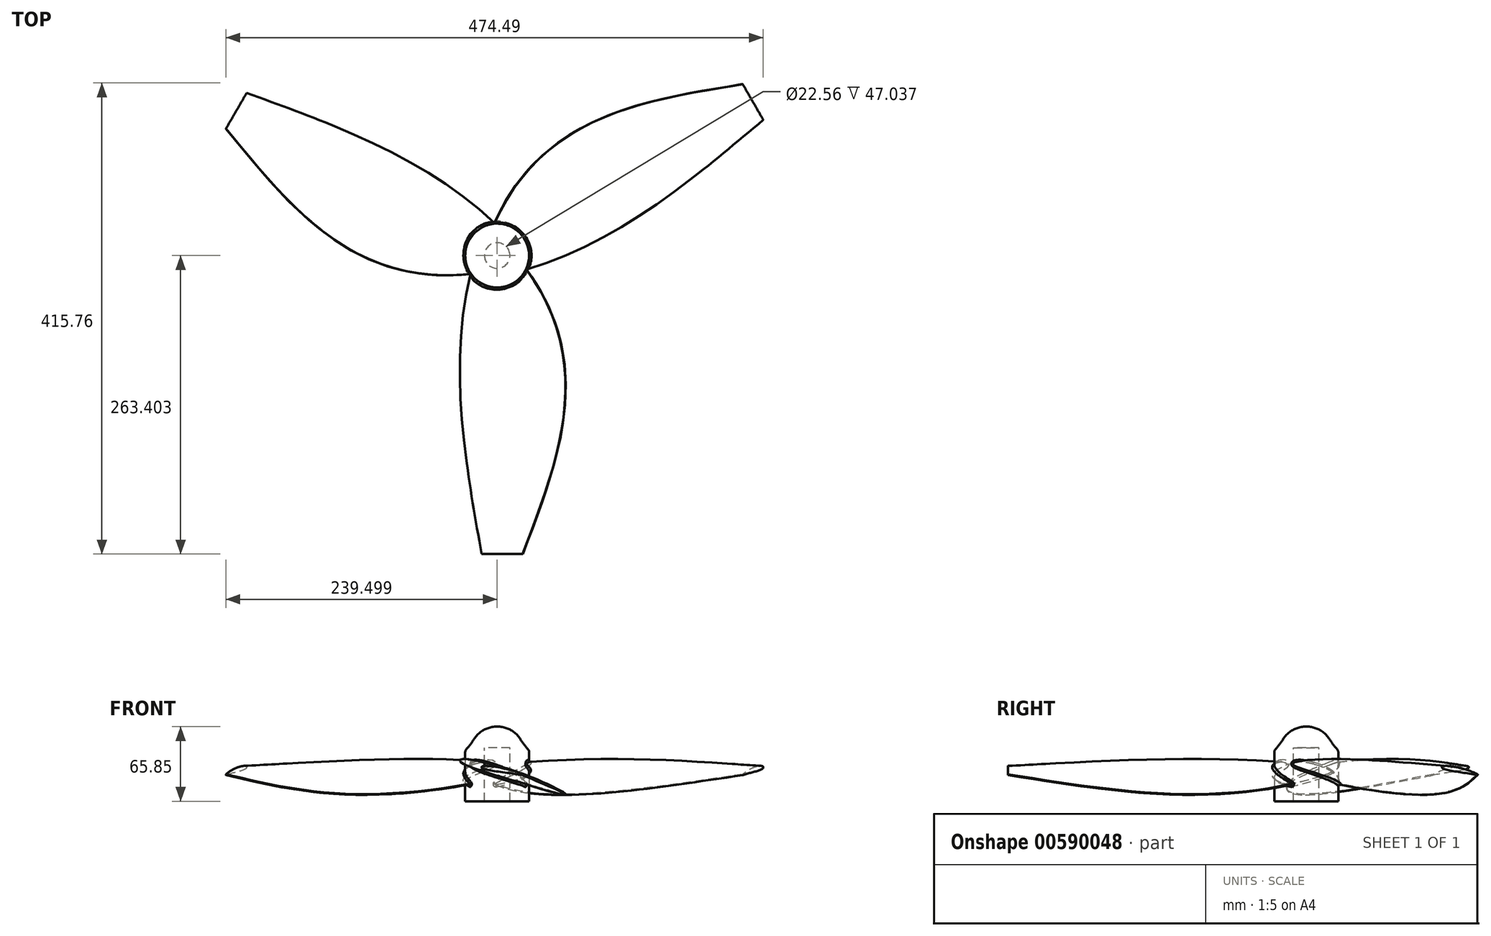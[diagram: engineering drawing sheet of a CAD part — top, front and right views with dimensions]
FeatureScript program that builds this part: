
annotation { "Feature Type Name" : "Feature", "Feature Type Description" : "" }
export const myFeature = defineFeature(function(context is Context, id is Id, definition is map)
    precondition{}
    {
        {
            var Q0;
            Q0=qCreatedBy(makeId("Front.planeOp"),FACE);
            var sketch = newSketch(context, id + "F0", { "sketchPlane" : qUnion([Q0])});
            skLineSegment(sketch, "E0", {"start": v(-25.68, 10.16) * mm, "end": v(0, 0) * mm, "construction": true});
            skLineSegment(sketch, "E1", {"start": v(0, 0) * mm, "end": v(25.68, -10.16) * mm, "construction": true});
            skLineSegment(sketch, "E2", {"start": v(25.68, -10.16) * mm, "end": v(51.36, -20.31) * mm, "construction": true});
            skLineSegment(sketch, "E3", {"start": v(51.36, -20.31) * mm, "end": v(77.03, -30.47) * mm, "construction": true});
            skLineSegment(sketch, "E4", {"start": v(0, 0) * mm, "end": v(3.73, 9.44) * mm, "construction": true});
            skLineSegment(sketch, "E5", {"start": v(-25.68, 10.16) * mm, "end": v(-23.81, 14.88) * mm, "construction": true});
            skFitSpline(sketch, "E6", {"points": [v(-25.68, 10.16) * mm, v(3.73, 9.44) * mm, v(77.03, -30.47) * mm], "startDerivative": vector(15.03, 38) * mm, "endDerivative": vector(104.92, -93.69) * mm});
            skPoint(sketch, "E7", {"position": v(1.87, 4.72) * mm});
            skLineSegment(sketch, "E8", {"start": v(-23.81, 14.88) * mm, "end": v(1.87, 4.72) * mm, "construction": true});
            skLineSegment(sketch, "E9", {"start": v(0, 0) * mm, "end": v(-1.87, -4.72) * mm, "construction": true});
            skLineSegment(sketch, "E10", {"start": v(-25.68, 10.16) * mm, "end": v(-27.54, 5.44) * mm, "construction": true});
            skFitSpline(sketch, "E11", {"points": [v(-25.68, 10.16) * mm, v(-1.87, -4.72) * mm, v(77.03, -30.47) * mm], "startDerivative": vector(-15.23, -38.5) * mm, "endDerivative": vector(121.84, -48.19) * mm});
            skLineSegment(sketch, "E12", {"start": v(51.36, -20.31) * mm, "end": v(55.09, -10.87) * mm, "construction": true});
            skSolve(sketch);
        }
        {
            var Q0;
            Q0=qCreatedBy(makeId("Front.planeOp"),FACE);
            cPlane(context, id + "F1", {"entities" : qUnion([Q0]), "cplaneType" : CPlaneType.OFFSET, "offset" : 50.8 * mm, "width" : 150 * mm, "height" : 150 * mm});
        }
        {
            var Q0;
            Q0=qCreatedBy(id+"F1.planeOp",FACE);
            var sketch = newSketch(context, id + "F2", { "sketchPlane" : qUnion([Q0])});
            skLineSegment(sketch, "E13", {"start": v(-38.33, 14.06) * mm, "end": v(0, 0) * mm, "construction": true});
            skLineSegment(sketch, "E14", {"start": v(0, 0) * mm, "end": v(38.33, -14.06) * mm, "construction": true});
            skLineSegment(sketch, "E15", {"start": v(38.33, -14.06) * mm, "end": v(76.67, -28.12) * mm, "construction": true});
            skLineSegment(sketch, "E16", {"start": v(76.67, -28.12) * mm, "end": v(115, -42.17) * mm, "construction": true});
            skLineSegment(sketch, "E17", {"start": v(0, 0) * mm, "end": v(4.06, 11.06) * mm, "construction": true});
            skLineSegment(sketch, "E18", {"start": v(-38.33, 14.06) * mm, "end": v(-36.3, 19.59) * mm, "construction": true});
            skFitSpline(sketch, "E19", {"points": [v(-38.33, 14.06) * mm, v(4.06, 11.06) * mm, v(115, -42.17) * mm], "startDerivative": vector(16.44, 44.82) * mm, "endDerivative": vector(163.27, -119.63) * mm});
            skPoint(sketch, "E20", {"position": v(2.03, 5.53) * mm});
            skLineSegment(sketch, "E21", {"start": v(-36.3, 19.59) * mm, "end": v(2.03, 5.53) * mm, "construction": true});
            skLineSegment(sketch, "E22", {"start": v(0, 0) * mm, "end": v(-2.03, -5.53) * mm, "construction": true});
            skLineSegment(sketch, "E23", {"start": v(-38.33, 14.06) * mm, "end": v(-40.36, 8.53) * mm, "construction": true});
            skFitSpline(sketch, "E24", {"points": [v(-38.33, 14.06) * mm, v(-2.03, -5.53) * mm, v(115, -42.17) * mm], "startDerivative": vector(-16.57, -45.19) * mm, "endDerivative": vector(181.7, -66.64) * mm});
            skLineSegment(sketch, "E25", {"start": v(76.67, -28.12) * mm, "end": v(80.72, -17.06) * mm, "construction": true});
            skSolve(sketch);
        }
        {
            var Q0;
            Q0=qCreatedBy(makeId("Front.planeOp"),FACE);
            cPlane(context, id + "F3", {"entities" : qUnion([Q0]), "cplaneType" : CPlaneType.OFFSET, "offset" : 711.2 * mm, "width" : 150 * mm, "height" : 150 * mm});
        }
        {
            var Q0;
            Q0=qCreatedBy(id+"F3.planeOp",FACE);
            var sketch = newSketch(context, id + "F4", { "sketchPlane" : qUnion([Q0])});
            skLineSegment(sketch, "E26", {"start": v(-10.03, 5.14) * mm, "end": v(16.27, 0) * mm, "construction": true});
            skLineSegment(sketch, "E27", {"start": v(16.27, 0) * mm, "end": v(42.56, -5.14) * mm, "construction": true});
            skLineSegment(sketch, "E28", {"start": v(42.56, -5.14) * mm, "end": v(68.86, -10.28) * mm, "construction": true});
            skLineSegment(sketch, "E29", {"start": v(68.86, -10.28) * mm, "end": v(95.16, -15.42) * mm, "construction": true});
            skLineSegment(sketch, "E30", {"start": v(16.27, 0) * mm, "end": v(17.61, 6.9) * mm, "construction": true});
            skLineSegment(sketch, "E31", {"start": v(-10.03, 5.14) * mm, "end": v(-9.36, 8.59) * mm, "construction": true});
            skFitSpline(sketch, "E32", {"points": [v(-10.03, 5.14) * mm, v(17.61, 6.9) * mm, v(95.16, -15.42) * mm], "startDerivative": vector(5.47, 28.01) * mm, "endDerivative": vector(118.7, -57.28) * mm});
            skPoint(sketch, "E33", {"position": v(16.94, 3.45) * mm});
            skLineSegment(sketch, "E34", {"start": v(-9.36, 8.59) * mm, "end": v(16.94, 3.45) * mm, "construction": true});
            skLineSegment(sketch, "E35", {"start": v(16.27, 0) * mm, "end": v(15.6, -3.45) * mm, "construction": true});
            skLineSegment(sketch, "E36", {"start": v(-10.03, 5.14) * mm, "end": v(-10.7, 1.7) * mm, "construction": true});
            skFitSpline(sketch, "E37", {"points": [v(-10.03, 5.14) * mm, v(15.6, -3.45) * mm, v(95.16, -15.42) * mm], "startDerivative": vector(-5.51, -28.2) * mm, "endDerivative": vector(124.61, -24.36) * mm});
            skLineSegment(sketch, "E38", {"start": v(68.86, -10.28) * mm, "end": v(70.2, -3.38) * mm, "construction": true});
            skSolve(sketch);
        }
        {
            var Q0;
            Q0=qSketchRegion(id+"F0",true);
            var Q1;
            Q1=qSketchRegion(id+"F2",true);
            var Q2;
            Q2=qSketchRegion(id+"F4",true);
            var Q3;
            Q3=sQuery(id+"F0.wireOp",VERTEX,"E6.1.internal");
            var Q4;
            Q4=sQuery(id+"F2.wireOp",VERTEX,"E19.1.internal");
            var Q5;
            Q5=sQuery(id+"F4.wireOp",VERTEX,"E30.end");
            loft(context, id + "F5", {"sheetProfilesArray" : [{ "sheetProfileEntities" : qUnion([Q0]) }, { "sheetProfileEntities" : qUnion([Q1]) }, { "sheetProfileEntities" : qUnion([Q2]) }], "matchConnections" : true, "connections" : [{ "connectionEntities" : qUnion([Q3, Q4, Q5]), "connectionEdgeQueries" : qUnion([]), "connectionEdgeParameters" : [] }]});
        }
        {
            var Q0;
            Q0=makeQuery(id+"F5.opLoft","SWEPT_EDGE",EDGE,{"disambiguationData":[OSD([sQuery(id+"F2.wireOp",EDGE,"E19"),sQuery(id+"F2.wireOp",EDGE,"E24"),sQuery(id+"F4.wireOp",EDGE,"E32"),sQuery(id+"F4.wireOp",EDGE,"E37")])]});
            fillet(context, id + "F6", {"entities" : qUnion([Q0]), "radius" : 1 * mm, "tangentPropagation" : true, "allowEdgeOverflow" : false});
        }
        {
            var Q0;
            Q0=qCreatedBy(makeId("Top.planeOp"),FACE);
            var sketch = newSketch(context, id + "F7", { "sketchPlane" : qUnion([Q0])});
            skCircle(sketch, "E39", {"center": v(27.04, 0) * mm, "radius": 76.2 * mm});
            skSolve(sketch);
        }
        {
            var Q0;
            Q0=qSketchRegion(id+"F7",true);
            extrude(context, id + "F8", {"entities" : qUnion([Q0]), "depth" : 50.8 * mm, "hasSecondDirection" : true, "secondDirectionOppositeDirection" : true, "secondDirectionDepth" : 76.2 * mm, "offsetDistance" : 25.4 * mm});
        }
        {
            var Q0;
            Q0=makeQuery(id+"F5.opLoft","SWEPT_BODY",BODY,{"disambiguationData":[OSD([makeQuery(id+"F0.imprint","IMPRINT",FACE,{"disambiguationData":[TD([[makeQuery(id+"F0.imprint","IMPRINT",EDGE,{"derivedFrom":sQuery(id+"F0.wireOp",EDGE,"E6")}),-1.0]])]}),sQuery(id+"F2.wireOp",EDGE,"E24"),makeQuery(id+"F4.imprint","IMPRINT",FACE,{"disambiguationData":[TD([[makeQuery(id+"F4.imprint","IMPRINT",EDGE,{"derivedFrom":sQuery(id+"F4.wireOp",EDGE,"E32")}),-1.0]])]})])]});
            var Q1;
            Q1=makeQuery(id+"F8.opExtrude","SWEPT_FACE",FACE,{"disambiguationData":[OSD([sQuery(id+"F7.wireOp",EDGE,"E39")])]});
            circularPattern(context, id + "F9", {"entities" : qUnion([Q0]), "axis" : qUnion([Q1]), "angle" : 360 * degree, "instanceCount" : 3, "equalSpace" : true});
        }
        {
            var Q0;
            Q0=makeQuery(id+"F9.opPattern","COPY",BODY,{"derivedFrom":makeQuery(id+"F5.opLoft","SWEPT_BODY",BODY,{"disambiguationData":[OSD([makeQuery(id+"F0.imprint","IMPRINT",FACE,{"disambiguationData":[TD([[makeQuery(id+"F0.imprint","IMPRINT",EDGE,{"derivedFrom":sQuery(id+"F0.wireOp",EDGE,"E6")}),-1.0]])]}),sQuery(id+"F2.wireOp",EDGE,"E24"),makeQuery(id+"F4.imprint","IMPRINT",FACE,{"disambiguationData":[TD([[makeQuery(id+"F4.imprint","IMPRINT",EDGE,{"derivedFrom":sQuery(id+"F4.wireOp",EDGE,"E32")}),-1.0]])]})])]}),"instanceName":"2"});
            var Q1;
            Q1=makeQuery(id+"F5.opLoft","SWEPT_BODY",BODY,{"disambiguationData":[OSD([makeQuery(id+"F0.imprint","IMPRINT",FACE,{"disambiguationData":[TD([[makeQuery(id+"F0.imprint","IMPRINT",EDGE,{"derivedFrom":sQuery(id+"F0.wireOp",EDGE,"E6")}),-1.0]])]}),sQuery(id+"F2.wireOp",EDGE,"E24"),makeQuery(id+"F4.imprint","IMPRINT",FACE,{"disambiguationData":[TD([[makeQuery(id+"F4.imprint","IMPRINT",EDGE,{"derivedFrom":sQuery(id+"F4.wireOp",EDGE,"E32")}),-1.0]])]})])]});
            var Q2;
            Q2=makeQuery(id+"F8.opExtrude","SWEPT_BODY",BODY,{"disambiguationData":[OSD([sQuery(id+"F7.wireOp",EDGE,"E39")])]});
            var Q3;
            Q3=makeQuery(id+"F9.opPattern","COPY",BODY,{"derivedFrom":makeQuery(id+"F5.opLoft","SWEPT_BODY",BODY,{"disambiguationData":[OSD([makeQuery(id+"F0.imprint","IMPRINT",FACE,{"disambiguationData":[TD([[makeQuery(id+"F0.imprint","IMPRINT",EDGE,{"derivedFrom":sQuery(id+"F0.wireOp",EDGE,"E6")}),-1.0]])]}),sQuery(id+"F2.wireOp",EDGE,"E24"),makeQuery(id+"F4.imprint","IMPRINT",FACE,{"disambiguationData":[TD([[makeQuery(id+"F4.imprint","IMPRINT",EDGE,{"derivedFrom":sQuery(id+"F4.wireOp",EDGE,"E32")}),-1.0]])]})])]}),"instanceName":"1"});
            var Q4;
            Q4=makeQuery(id+"F9.opPattern","COPY",BODY,{"derivedFrom":makeQuery(id+"F5.opLoft","SWEPT_BODY",BODY,{"disambiguationData":[OSD([makeQuery(id+"F0.imprint","IMPRINT",FACE,{"disambiguationData":[TD([[makeQuery(id+"F0.imprint","IMPRINT",EDGE,{"derivedFrom":sQuery(id+"F0.wireOp",EDGE,"E6")}),-1.0]])]}),sQuery(id+"F2.wireOp",EDGE,"E24"),makeQuery(id+"F4.imprint","IMPRINT",FACE,{"disambiguationData":[TD([[makeQuery(id+"F4.imprint","IMPRINT",EDGE,{"derivedFrom":sQuery(id+"F4.wireOp",EDGE,"E32")}),-1.0]])]})])]}),"instanceName":"4"});
            var Q5;
            Q5=makeQuery(id+"F9.opPattern","COPY",BODY,{"derivedFrom":makeQuery(id+"F5.opLoft","SWEPT_BODY",BODY,{"disambiguationData":[OSD([makeQuery(id+"F0.imprint","IMPRINT",FACE,{"disambiguationData":[TD([[makeQuery(id+"F0.imprint","IMPRINT",EDGE,{"derivedFrom":sQuery(id+"F0.wireOp",EDGE,"E6")}),-1.0]])]}),sQuery(id+"F2.wireOp",EDGE,"E24"),makeQuery(id+"F4.imprint","IMPRINT",FACE,{"disambiguationData":[TD([[makeQuery(id+"F4.imprint","IMPRINT",EDGE,{"derivedFrom":sQuery(id+"F4.wireOp",EDGE,"E32")}),-1.0]])]})])]}),"instanceName":"3"});
            booleanBodies(context, id + "F10", {"operationType" : BooleanOperationType.UNION, "tools" : qUnion([Q0, Q1, Q2, Q3, Q4, Q5])});
        }
        {
            var Q0;
            Q0=makeQuery(id+"F8.opExtrude","CAP_FACE",FACE,{"disambiguationData":[OSD([sQuery(id+"F7.wireOp",EDGE,"E39")])],"isStart":false});
            var sketch = newSketch(context, id + "F11", { "sketchPlane" : qUnion([Q0])});
            skCircle(sketch, "E40", {"center": v(27.04, 0) * mm, "radius": 30.45 * mm});
            skSolve(sketch);
        }
        {
            var Q0;
            Q0=qSketchRegion(id+"F11",true);
            extrude(context, id + "F12", {"entities" : qUnion([Q0]), "operationType" : NewBodyOperationType.REMOVE, "endBound" : BoundingType.THROUGH_ALL, "oppositeDirection" : true, "depth" : 25 * mm});
        }
        {
            var Q0;
            {var subQ0=sQuery(id+"F0.wireOp",VERTEX,"E6.1.internal");var subQ1=sQuery(id+"F0.wireOp",EDGE,"E6");var subQ2=sQuery(id+"F0.wireOp",EDGE,"E11");var subQ3=sQuery(id+"F2.wireOp",VERTEX,"E19.1.internal");var subQ4=sQuery(id+"F2.wireOp",EDGE,"E19");var subQ5=sQuery(id+"F2.wireOp",EDGE,"E24");Q0=makeQuery(id+"F10.opBoolean","INTERSECT",EDGE,{"derivedFrom":[makeQuery(id+"F8.opExtrude","SWEPT_FACE",FACE,{"disambiguationData":[OSD([sQuery(id+"F7.wireOp",EDGE,"E39")])]}),makeQuery(id+"F9.opPattern","COPY",FACE,{"derivedFrom":makeQuery(id+"F5.opLoft","SWEPT_FACE",FACE,{"disambiguationData":[OSD([subQ0,subQ1,subQ2,subQ3,subQ4,subQ5]),TDD([subQ0,makeQuery(id+"F0.imprint","INTERSECT",VERTEX,{"disambiguationData":[OD(0.0)],"derivedFrom":[subQ1,subQ2]}),makeQuery(id+"F0.imprint","IMPRINT",EDGE,{"derivedFrom":subQ1}),subQ3,makeQuery(id+"F2.imprint","INTERSECT",VERTEX,{"disambiguationData":[OD(0.0)],"derivedFrom":[subQ4,subQ5]}),makeQuery(id+"F2.imprint","IMPRINT",EDGE,{"derivedFrom":subQ4})])]}),"instanceName":"2"})]});}
            var Q1;
            {var subQ0=sQuery(id+"F0.wireOp",VERTEX,"E6.1.internal");var subQ1=sQuery(id+"F0.wireOp",EDGE,"E6");var subQ2=sQuery(id+"F0.wireOp",EDGE,"E11");var subQ3=sQuery(id+"F2.wireOp",VERTEX,"E19.1.internal");var subQ4=sQuery(id+"F2.wireOp",EDGE,"E19");var subQ5=sQuery(id+"F2.wireOp",EDGE,"E24");Q1=makeQuery(id+"F10.opBoolean","INTERSECT",EDGE,{"derivedFrom":[makeQuery(id+"F5.opLoft","SWEPT_FACE",FACE,{"disambiguationData":[OSD([subQ0,subQ1,subQ2,subQ3,subQ4,subQ5]),TDD([subQ0,makeQuery(id+"F0.imprint","INTERSECT",VERTEX,{"disambiguationData":[OD(1.0)],"derivedFrom":[subQ1,subQ2]}),makeQuery(id+"F0.imprint","IMPRINT",EDGE,{"derivedFrom":subQ1}),subQ3,makeQuery(id+"F2.imprint","INTERSECT",VERTEX,{"disambiguationData":[OD(1.0)],"derivedFrom":[subQ4,subQ5]}),makeQuery(id+"F2.imprint","IMPRINT",EDGE,{"derivedFrom":subQ4})])]}),makeQuery(id+"F8.opExtrude","SWEPT_FACE",FACE,{"disambiguationData":[OSD([sQuery(id+"F7.wireOp",EDGE,"E39")])]})]});}
            var Q2;
            {var subQ0=sQuery(id+"F0.wireOp",VERTEX,"E6.1.internal");var subQ1=sQuery(id+"F0.wireOp",EDGE,"E6");var subQ2=sQuery(id+"F0.wireOp",EDGE,"E11");var subQ3=sQuery(id+"F2.wireOp",VERTEX,"E19.1.internal");var subQ4=sQuery(id+"F2.wireOp",EDGE,"E19");var subQ5=sQuery(id+"F2.wireOp",EDGE,"E24");Q2=makeQuery(id+"F10.opBoolean","INTERSECT",EDGE,{"derivedFrom":[makeQuery(id+"F8.opExtrude","SWEPT_FACE",FACE,{"disambiguationData":[OSD([sQuery(id+"F7.wireOp",EDGE,"E39")])]}),makeQuery(id+"F9.opPattern","COPY",FACE,{"derivedFrom":makeQuery(id+"F5.opLoft","SWEPT_FACE",FACE,{"disambiguationData":[OSD([subQ0,subQ1,subQ2,subQ3,subQ4,subQ5]),TDD([subQ0,makeQuery(id+"F0.imprint","INTERSECT",VERTEX,{"disambiguationData":[OD(1.0)],"derivedFrom":[subQ1,subQ2]}),makeQuery(id+"F0.imprint","IMPRINT",EDGE,{"derivedFrom":subQ1}),subQ3,makeQuery(id+"F2.imprint","INTERSECT",VERTEX,{"disambiguationData":[OD(1.0)],"derivedFrom":[subQ4,subQ5]}),makeQuery(id+"F2.imprint","IMPRINT",EDGE,{"derivedFrom":subQ4})])]}),"instanceName":"1"})]});}
            var Q3;
            {var subQ0=sQuery(id+"F0.wireOp",VERTEX,"E6.1.internal");var subQ1=sQuery(id+"F0.wireOp",EDGE,"E6");var subQ2=sQuery(id+"F0.wireOp",EDGE,"E11");var subQ3=sQuery(id+"F2.wireOp",VERTEX,"E19.1.internal");var subQ4=sQuery(id+"F2.wireOp",EDGE,"E19");var subQ5=sQuery(id+"F2.wireOp",EDGE,"E24");Q3=makeQuery(id+"F10.opBoolean","INTERSECT",EDGE,{"derivedFrom":[makeQuery(id+"F8.opExtrude","SWEPT_FACE",FACE,{"disambiguationData":[OSD([sQuery(id+"F7.wireOp",EDGE,"E39")])]}),makeQuery(id+"F9.opPattern","COPY",FACE,{"derivedFrom":makeQuery(id+"F5.opLoft","SWEPT_FACE",FACE,{"disambiguationData":[OSD([subQ0,subQ1,subQ2,subQ3,subQ4,subQ5]),TDD([subQ0,makeQuery(id+"F0.imprint","INTERSECT",VERTEX,{"disambiguationData":[OD(1.0)],"derivedFrom":[subQ1,subQ2]}),makeQuery(id+"F0.imprint","IMPRINT",EDGE,{"derivedFrom":subQ1}),subQ3,makeQuery(id+"F2.imprint","INTERSECT",VERTEX,{"disambiguationData":[OD(1.0)],"derivedFrom":[subQ4,subQ5]}),makeQuery(id+"F2.imprint","IMPRINT",EDGE,{"derivedFrom":subQ4})])]}),"instanceName":"4"})]});}
            var Q4;
            {var subQ0=sQuery(id+"F0.wireOp",VERTEX,"E6.1.internal");var subQ1=sQuery(id+"F0.wireOp",EDGE,"E6");var subQ2=sQuery(id+"F0.wireOp",EDGE,"E11");var subQ3=sQuery(id+"F2.wireOp",VERTEX,"E19.1.internal");var subQ4=sQuery(id+"F2.wireOp",EDGE,"E19");var subQ5=sQuery(id+"F2.wireOp",EDGE,"E24");Q4=makeQuery(id+"F10.opBoolean","INTERSECT",EDGE,{"derivedFrom":[makeQuery(id+"F8.opExtrude","SWEPT_FACE",FACE,{"disambiguationData":[OSD([sQuery(id+"F7.wireOp",EDGE,"E39")])]}),makeQuery(id+"F9.opPattern","COPY",FACE,{"derivedFrom":makeQuery(id+"F5.opLoft","SWEPT_FACE",FACE,{"disambiguationData":[OSD([subQ0,subQ1,subQ2,subQ3,subQ4,subQ5]),TDD([subQ0,makeQuery(id+"F0.imprint","INTERSECT",VERTEX,{"disambiguationData":[OD(0.0)],"derivedFrom":[subQ1,subQ2]}),makeQuery(id+"F0.imprint","IMPRINT",EDGE,{"derivedFrom":subQ1}),subQ3,makeQuery(id+"F2.imprint","INTERSECT",VERTEX,{"disambiguationData":[OD(0.0)],"derivedFrom":[subQ4,subQ5]}),makeQuery(id+"F2.imprint","IMPRINT",EDGE,{"derivedFrom":subQ4})])]}),"instanceName":"3"})]});}
            fillet(context, id + "F13", {"entities" : qUnion([Q0, Q1, Q2, Q3, Q4]), "radius" : 5 * mm, "tangentPropagation" : true, "allowEdgeOverflow" : false});
        }
        {
            var Q0;
            Q0=makeQuery(id+"F8.opExtrude","CAP_EDGE",EDGE,{"disambiguationData":[OSD([sQuery(id+"F7.wireOp",EDGE,"E39")])],"isStart":false});
            fillet(context, id + "F14", {"entities" : qUnion([Q0]), "radius" : 10 * mm, "tangentPropagation" : true, "allowEdgeOverflow" : false});
        }
        {
            var Q0;
            Q0=makeQuery(id+"F8.opExtrude","CAP_FACE",FACE,{"disambiguationData":[OSD([sQuery(id+"F7.wireOp",EDGE,"E39")])],"isStart":false});
            var sketch = newSketch(context, id + "F15", { "sketchPlane" : qUnion([Q0])});
            skCircle(sketch, "E41", {"center": v(27.04, 0) * mm, "radius": 63.5 * mm});
            skSolve(sketch);
        }
        {
            var Q0;
            Q0=qSketchRegion(id+"F15",true);
            extrude(context, id + "F16", {"entities" : qUnion([Q0]), "operationType" : NewBodyOperationType.ADD, "depth" : 50.8 * mm, "offsetDistance" : 25.4 * mm});
        }
        {
            var Q0;
            Q0=makeQuery(id+"F16.opExtrude","CAP_EDGE",EDGE,{"disambiguationData":[OSD([sQuery(id+"F15.wireOp",EDGE,"E41")])],"isStart":false});
            fillet(context, id + "F17", {"entities" : qUnion([Q0]), "radius" : 63.5 * mm, "tangentPropagation" : true, "allowEdgeOverflow" : false});
        }
        {
            var Q0;
            Q0=makeQuery(id+"F17.opFillet","BLEND_EDGE",EDGE,{"blendedFrom":[makeQuery(id+"F16.opExtrude","CAP_EDGE",EDGE,{"disambiguationData":[OSD([sQuery(id+"F15.wireOp",EDGE,"E41")])],"isStart":false}),makeQuery(id+"F8.opExtrude","CAP_FACE",FACE,{"disambiguationData":[OSD([sQuery(id+"F7.wireOp",EDGE,"E39")])],"isStart":false})],"blendedInto":[makeQuery(id+"F8.opExtrude","CAP_FACE",FACE,{"disambiguationData":[OSD([sQuery(id+"F7.wireOp",EDGE,"E39")])],"isStart":false})]});
            fillet(context, id + "F18", {"entities" : qUnion([Q0]), "radius" : 254 * mm, "tangentPropagation" : true, "allowEdgeOverflow" : false});
        }
        {
            var Q0;
            Q0=makeQuery(id+"F9.opPattern","COPY",BODY,{"derivedFrom":makeQuery(id+"F5.opLoft","SWEPT_BODY",BODY,{"disambiguationData":[OSD([makeQuery(id+"F0.imprint","IMPRINT",FACE,{"disambiguationData":[TD([[makeQuery(id+"F0.imprint","IMPRINT",EDGE,{"derivedFrom":sQuery(id+"F0.wireOp",EDGE,"E6")}),-1.0]])]}),sQuery(id+"F2.wireOp",EDGE,"E19"),makeQuery(id+"F4.imprint","IMPRINT",FACE,{"disambiguationData":[TD([[makeQuery(id+"F4.imprint","IMPRINT",EDGE,{"derivedFrom":sQuery(id+"F4.wireOp",EDGE,"E32")}),-1.0]])]})])]}),"instanceName":"2"});
            var Q1;
            {var subQ0=sQuery(id+"F2.wireOp",EDGE,"E19");var subQ1=sQuery(id+"F2.wireOp",EDGE,"E24");var subQ2=sQuery(id+"F2.wireOp",VERTEX,"E19.1.internal");var subQ3=sQuery(id+"F0.wireOp",EDGE,"E6");var subQ4=sQuery(id+"F0.wireOp",EDGE,"E11");var subQ5=sQuery(id+"F0.wireOp",VERTEX,"E6.1.internal");var subQ6=makeQuery(id+"F5.opLoft","SWEPT_FACE",FACE,{"disambiguationData":[OSD([subQ5,subQ3,subQ4,subQ2,subQ0,subQ1]),TDD([subQ5,makeQuery(id+"F0.imprint","INTERSECT",VERTEX,{"disambiguationData":[OD(1.0)],"derivedFrom":[subQ3,subQ4]}),makeQuery(id+"F0.imprint","IMPRINT",EDGE,{"derivedFrom":subQ3}),subQ2,makeQuery(id+"F2.imprint","INTERSECT",VERTEX,{"disambiguationData":[OD(1.0)],"derivedFrom":[subQ0,subQ1]}),makeQuery(id+"F2.imprint","IMPRINT",EDGE,{"derivedFrom":subQ0})])]});var subQ7=makeQuery(id+"F6.opFillet","BLEND_FACE",FACE,{"disambiguationData":[OSD([subQ0,subQ1,sQuery(id+"F4.wireOp",EDGE,"E32"),sQuery(id+"F4.wireOp",EDGE,"E37")])]});var subQ8=makeQuery(id+"F8.opExtrude","SWEPT_FACE",FACE,{"disambiguationData":[OSD([sQuery(id+"F7.wireOp",EDGE,"E39")])]});Q1=makeQuery(id+"F13.opFillet","BLEND_VERTEX",VERTEX,{"blendedFrom":[makeQuery(id+"F10.opBoolean","INTERSECT",EDGE,{"derivedFrom":[subQ7,subQ8]}),makeQuery(id+"F10.opBoolean","INTERSECT",EDGE,{"derivedFrom":[subQ6,subQ8]}),subQ7,subQ6],"blendedInto":[subQ7,subQ6]});}
            transform(context, id + "F19", {"entities" : qUnion([Q0]), "transformType" : TransformType.SCALE_UNIFORMLY, "scale" : .37037037, "scalePoint" : qUnion([Q1]), "makeCopy" : false});
        }
    });
